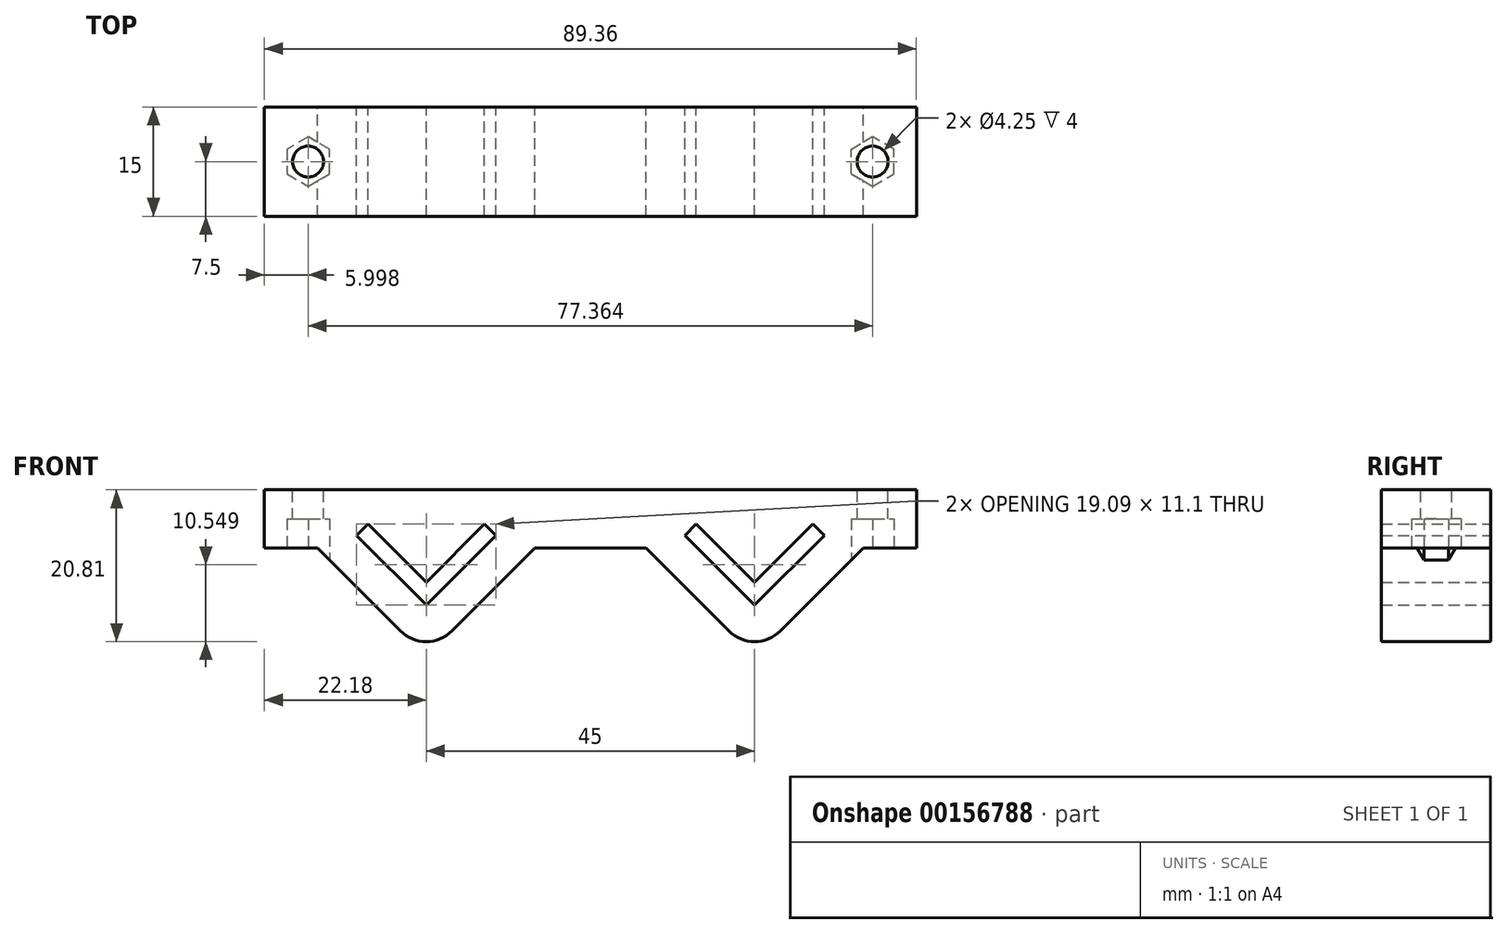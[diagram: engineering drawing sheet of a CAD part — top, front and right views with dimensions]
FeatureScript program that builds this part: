
annotation { "Feature Type Name" : "Feature", "Feature Type Description" : "" }
export const myFeature = defineFeature(function(context is Context, id is Id, definition is map)
    precondition{}
    {
        {
            var Q0;
            Q0=qCreatedBy(makeId("Front.planeOp"),FACE);
            var sketch = newSketch(context, id + "F0", { "sketchPlane" : qUnion([Q0])});
            skLineSegment(sketch, "E0.bottom", {"start": v(7.5, -12.7) * mm, "end": v(-7.5, -12.7) * mm, "construction": true});
            skLineSegment(sketch, "E0.top", {"start": v(15.32, 12.7) * mm, "end": v(-14.68, 12.7) * mm});
            skLineSegment(sketch, "E0.right", {"start": v(-14.88, 4.7) * mm, "end": v(-14.88, 4.7) * mm});
            skPoint(sketch, "E0.middle", {"position": v(0, 0) * mm});
            skLineSegment(sketch, "E1", {"start": v(-8, 8) * mm, "end": v(0, 0) * mm});
            skLineSegment(sketch, "E2", {"start": v(0, 0) * mm, "end": v(8, 8) * mm});
            skLineSegment(sketch, "E3", {"start": v(8, 8) * mm, "end": v(9.55, 6.43) * mm});
            skLineSegment(sketch, "E4", {"start": v(9.55, 6.43) * mm, "end": v(0, -3.11) * mm});
            skLineSegment(sketch, "E5", {"start": v(0, -3.11) * mm, "end": v(-9.55, 6.43) * mm});
            skLineSegment(sketch, "E6", {"start": v(-9.55, 6.43) * mm, "end": v(-8, 8) * mm});
            skLineSegment(sketch, "E7", {"start": v(-14.88, 4.7) * mm, "end": v(-7.5, -2.68) * mm});
            skLineSegment(sketch, "E8", {"start": v(-7.5, -2.68) * mm, "end": v(-7.5, -12.7) * mm, "construction": true});
            skLineSegment(sketch, "E9.MirrorCS", {"start": v(14.88, 4.7) * mm, "end": v(7.5, -2.68) * mm});
            skLineSegment(sketch, "E10.MirrorCS", {"start": v(7.5, -2.68) * mm, "end": v(7.5, -12.7) * mm, "construction": true});
            skPoint(sketch, "E11.orphan", {"position": v(-15.32, -12.7) * mm});
            skPoint(sketch, "E12.orphan", {"position": v(14.68, -12.7) * mm});
            skLineSegment(sketch, "E13", {"start": v(-7.5, -2.68) * mm, "end": v(0, -10.18) * mm});
            skLineSegment(sketch, "E14", {"start": v(0, -10.18) * mm, "end": v(7.5, -2.68) * mm});
            skLineSegment(sketch, "E15", {"start": v(-14.68, 12.7) * mm, "end": v(-22.18, 12.7) * mm});
            skLineSegment(sketch, "E16", {"start": v(-22.18, 12.7) * mm, "end": v(-22.18, 4.7) * mm});
            skLineSegment(sketch, "E17", {"start": v(-22.18, 4.7) * mm, "end": v(-14.88, 4.7) * mm});
            skLineSegment(sketch, "E18.MirrorCS", {"start": v(14.68, 12.7) * mm, "end": v(22.18, 12.7) * mm});
            skLineSegment(sketch, "E19", {"start": v(22.5, 0) * mm, "end": v(22.5, 15.9) * mm, "construction": true});
            skLineSegment(sketch, "E20.MirrorCS", {"start": v(59.88, 4.7) * mm, "end": v(59.88, 4.7) * mm});
            skLineSegment(sketch, "E21.MirrorCS", {"start": v(37, 8) * mm, "end": v(35.45, 6.43) * mm});
            skLineSegment(sketch, "E22.MirrorCS", {"start": v(54.55, 6.43) * mm, "end": v(53, 8) * mm});
            skLineSegment(sketch, "E23.MirrorCS", {"start": v(29.68, 12.7) * mm, "end": v(59.68, 12.7) * mm});
            skLineSegment(sketch, "E24.MirrorCS", {"start": v(59.68, 12.7) * mm, "end": v(67.18, 12.7) * mm});
            skLineSegment(sketch, "E25.MirrorCS", {"start": v(45, 0) * mm, "end": v(37, 8) * mm});
            skPoint(sketch, "E26.MirrorP", {"position": v(30.32, -12.7) * mm});
            skLineSegment(sketch, "E27.MirrorCS", {"start": v(35.45, 6.43) * mm, "end": v(45, -3.11) * mm});
            skLineSegment(sketch, "E28.MirrorCS", {"start": v(59.88, 4.7) * mm, "end": v(52.5, -2.68) * mm});
            skLineSegment(sketch, "E29.MirrorCS", {"start": v(52.5, -2.68) * mm, "end": v(52.5, -12.7) * mm, "construction": true});
            skLineSegment(sketch, "E30.MirrorCS", {"start": v(30.12, 4.7) * mm, "end": v(37.5, -2.68) * mm});
            skLineSegment(sketch, "E31.MirrorCS", {"start": v(67.18, 4.7) * mm, "end": v(59.88, 4.7) * mm});
            skPoint(sketch, "E32.MirrorP", {"position": v(45, 0) * mm});
            skLineSegment(sketch, "E33.MirrorCS", {"start": v(37.5, -12.7) * mm, "end": v(52.5, -12.7) * mm, "construction": true});
            skLineSegment(sketch, "E34.MirrorCS", {"start": v(37.5, -2.68) * mm, "end": v(37.5, -12.7) * mm, "construction": true});
            skLineSegment(sketch, "E35.MirrorCS", {"start": v(67.18, 12.7) * mm, "end": v(67.18, 4.7) * mm});
            skLineSegment(sketch, "E36.MirrorCS", {"start": v(52.5, -2.68) * mm, "end": v(45, -10.18) * mm});
            skLineSegment(sketch, "E37.MirrorCS", {"start": v(45, -10.18) * mm, "end": v(37.5, -2.68) * mm});
            skPoint(sketch, "E38.MirrorP", {"position": v(60.32, -12.7) * mm});
            skLineSegment(sketch, "E39.MirrorCS", {"start": v(53, 8) * mm, "end": v(45, 0) * mm});
            skLineSegment(sketch, "E40.MirrorCS", {"start": v(45, -3.11) * mm, "end": v(54.55, 6.43) * mm});
            skLineSegment(sketch, "E41.MirrorCS", {"start": v(30.32, 12.7) * mm, "end": v(22.82, 12.7) * mm});
            skLineSegment(sketch, "E42", {"start": v(14.88, 4.7) * mm, "end": v(30.12, 4.7) * mm});
            skLineSegment(sketch, "E43", {"start": v(22.18, 12.7) * mm, "end": v(22.82, 12.7) * mm});
            skLineSegment(sketch, "E44", {"start": v(-16.18, 12.7) * mm, "end": v(-16.18, 4.7) * mm, "construction": true});
            skSolve(sketch);
        }
        {
            var Q0;
            Q0=qSketchRegion(id+"F0",true);
            extrude(context, id + "F1", {"entities" : qUnion([Q0]), "depth" : 15 * mm});
        }
        {
            var Q0;
            Q0=makeQuery(id+"F1.opExtrude","SWEPT_FACE",FACE,{"disambiguationData":[OSD([sQuery(id+"F0.wireOp",EDGE,"E0.top"),sQuery(id+"F0.wireOp",EDGE,"E15"),sQuery(id+"F0.wireOp",EDGE,"E18.MirrorCS")])]});
            var sketch = newSketch(context, id + "F2", { "sketchPlane" : qUnion([Q0])});
            skCircle(sketch, "E45", {"center": v(-16.18, -7.5) * mm, "radius": 2.12 * mm});
            skCircle(sketch, "E46", {"center": v(61.18, -7.5) * mm, "radius": 2.12 * mm});
            skSolve(sketch);
        }
        {
            var Q0;
            Q0=qSketchRegion(id+"F2",true);
            extrude(context, id + "F3", {"entities" : qUnion([Q0]), "operationType" : NewBodyOperationType.REMOVE, "oppositeDirection" : true, "depth" : 25 * mm});
        }
        {
            var Q0;
            Q0=makeQuery(id+"F1.opExtrude","SWEPT_FACE",FACE,{"disambiguationData":[OSD([sQuery(id+"F0.wireOp",EDGE,"E17")])]});
            var sketch = newSketch(context, id + "F4", { "sketchPlane" : qUnion([Q0])});
            skCircle(sketch, "E47.cCircle", {"center": v(-16.18, 7.5) * mm, "radius": 2.93 * mm, "construction": true});
            skLineSegment(sketch, "E47.0", {"start": v(-19.1, 5.81) * mm, "end": v(-19.1, 9.19) * mm});
            skLineSegment(sketch, "E47.1", {"start": v(-19.1, 9.19) * mm, "end": v(-16.18, 10.88) * mm});
            skLineSegment(sketch, "E47.2", {"start": v(-16.18, 10.88) * mm, "end": v(-13.26, 9.19) * mm});
            skLineSegment(sketch, "E47.3", {"start": v(-13.26, 9.19) * mm, "end": v(-13.26, 5.81) * mm});
            skLineSegment(sketch, "E47.4", {"start": v(-13.26, 5.81) * mm, "end": v(-16.18, 4.12) * mm});
            skLineSegment(sketch, "E47.5", {"start": v(-16.18, 4.12) * mm, "end": v(-19.1, 5.81) * mm});
            skPoint(sketch, "E47.0.midPoint", {"position": v(-19.1, 7.5) * mm});
            skCircle(sketch, "E48.cCircle", {"center": v(61.18, 7.5) * mm, "radius": 2.92 * mm, "construction": true});
            skLineSegment(sketch, "E48.0", {"start": v(64.1, 9.19) * mm, "end": v(64.1, 5.81) * mm});
            skLineSegment(sketch, "E48.1", {"start": v(64.1, 5.81) * mm, "end": v(61.18, 4.12) * mm});
            skLineSegment(sketch, "E48.2", {"start": v(61.18, 4.12) * mm, "end": v(58.26, 5.81) * mm});
            skLineSegment(sketch, "E48.3", {"start": v(58.26, 5.81) * mm, "end": v(58.26, 9.19) * mm});
            skLineSegment(sketch, "E48.4", {"start": v(58.26, 9.19) * mm, "end": v(61.18, 10.88) * mm});
            skLineSegment(sketch, "E48.5", {"start": v(61.18, 10.88) * mm, "end": v(64.1, 9.19) * mm});
            skPoint(sketch, "E48.0.midPoint", {"position": v(64.1, 7.5) * mm});
            skSolve(sketch);
        }
        {
            var Q0;
            Q0=qSketchRegion(id+"F4",true);
            extrude(context, id + "F5", {"entities" : qUnion([Q0]), "operationType" : NewBodyOperationType.REMOVE, "oppositeDirection" : true, "depth" : 4 * mm});
        }
        {
            var Q0;
            Q0=makeQuery(id+"F1.opExtrude","SWEPT_EDGE",EDGE,{"disambiguationData":[OSD([sQuery(id+"F0.wireOp",EDGE,"E13"),sQuery(id+"F0.wireOp",EDGE,"E14")])]});
            var Q1;
            Q1=makeQuery(id+"F1.opExtrude","SWEPT_EDGE",EDGE,{"disambiguationData":[OSD([sQuery(id+"F0.wireOp",EDGE,"E36.MirrorCS"),sQuery(id+"F0.wireOp",EDGE,"E37.MirrorCS")])]});
            fillet(context, id + "F6", {"entities" : qUnion([Q0, Q1]), "radius" : 5 * mm, "tangentPropagation" : true, "allowEdgeOverflow" : false});
        }
        {
            var Q0;
            Q0=makeQuery(id+"F5.boolean.opBoolean","COPY",FACE,{"derivedFrom":makeQuery(id+"F5.opExtrude","CAP_FACE",FACE,{"disambiguationData":[OSD([sQuery(id+"F4.wireOp",EDGE,"E47.0"),sQuery(id+"F4.wireOp",EDGE,"E47.1"),sQuery(id+"F4.wireOp",EDGE,"E47.2"),sQuery(id+"F4.wireOp",EDGE,"E47.3"),sQuery(id+"F4.wireOp",EDGE,"E47.4"),sQuery(id+"F4.wireOp",EDGE,"E47.5")])],"isStart":false})});
            var sketch = newSketch(context, id + "F7", { "sketchPlane" : qUnion([Q0])});
            skCircle(sketch, "E49.cCircle", {"center": v(-16.18, 7.5) * mm, "radius": 2.92 * mm, "construction": true});
            skLineSegment(sketch, "E49.0", {"start": v(-19.1, 5.81) * mm, "end": v(-19.1, 9.19) * mm});
            skLineSegment(sketch, "E49.1", {"start": v(-19.1, 9.19) * mm, "end": v(-16.18, 10.88) * mm});
            skLineSegment(sketch, "E49.2", {"start": v(-16.18, 10.88) * mm, "end": v(-13.26, 9.19) * mm});
            skLineSegment(sketch, "E49.3", {"start": v(-13.26, 9.19) * mm, "end": v(-13.26, 5.81) * mm});
            skLineSegment(sketch, "E49.4", {"start": v(-13.26, 5.81) * mm, "end": v(-16.18, 4.12) * mm});
            skLineSegment(sketch, "E49.5", {"start": v(-16.18, 4.12) * mm, "end": v(-19.1, 5.81) * mm});
            skPoint(sketch, "E49.0.midPoint", {"position": v(-19.1, 7.5) * mm});
            skCircle(sketch, "E50.cCircle", {"center": v(61.18, 7.5) * mm, "radius": 2.92 * mm, "construction": true});
            skLineSegment(sketch, "E50.0", {"start": v(64.1, 9.19) * mm, "end": v(64.1, 5.81) * mm});
            skLineSegment(sketch, "E50.1", {"start": v(64.1, 5.81) * mm, "end": v(61.18, 4.12) * mm});
            skLineSegment(sketch, "E50.2", {"start": v(61.18, 4.12) * mm, "end": v(58.26, 5.81) * mm});
            skLineSegment(sketch, "E50.3", {"start": v(58.26, 5.81) * mm, "end": v(58.26, 9.19) * mm});
            skLineSegment(sketch, "E50.4", {"start": v(58.26, 9.19) * mm, "end": v(61.18, 10.88) * mm});
            skLineSegment(sketch, "E50.5", {"start": v(61.18, 10.88) * mm, "end": v(64.1, 9.19) * mm});
            skPoint(sketch, "E50.0.midPoint", {"position": v(64.1, 7.5) * mm});
            skSolve(sketch);
        }
        {
            var Q0;
            Q0 = qSketchRegion(id + "F7", true);
            extrude(context, id + "F8", {"entities" : qUnion([Q0]), "operationType" : NewBodyOperationType.REMOVE, "depth" : 25 * mm});
        }
    });
